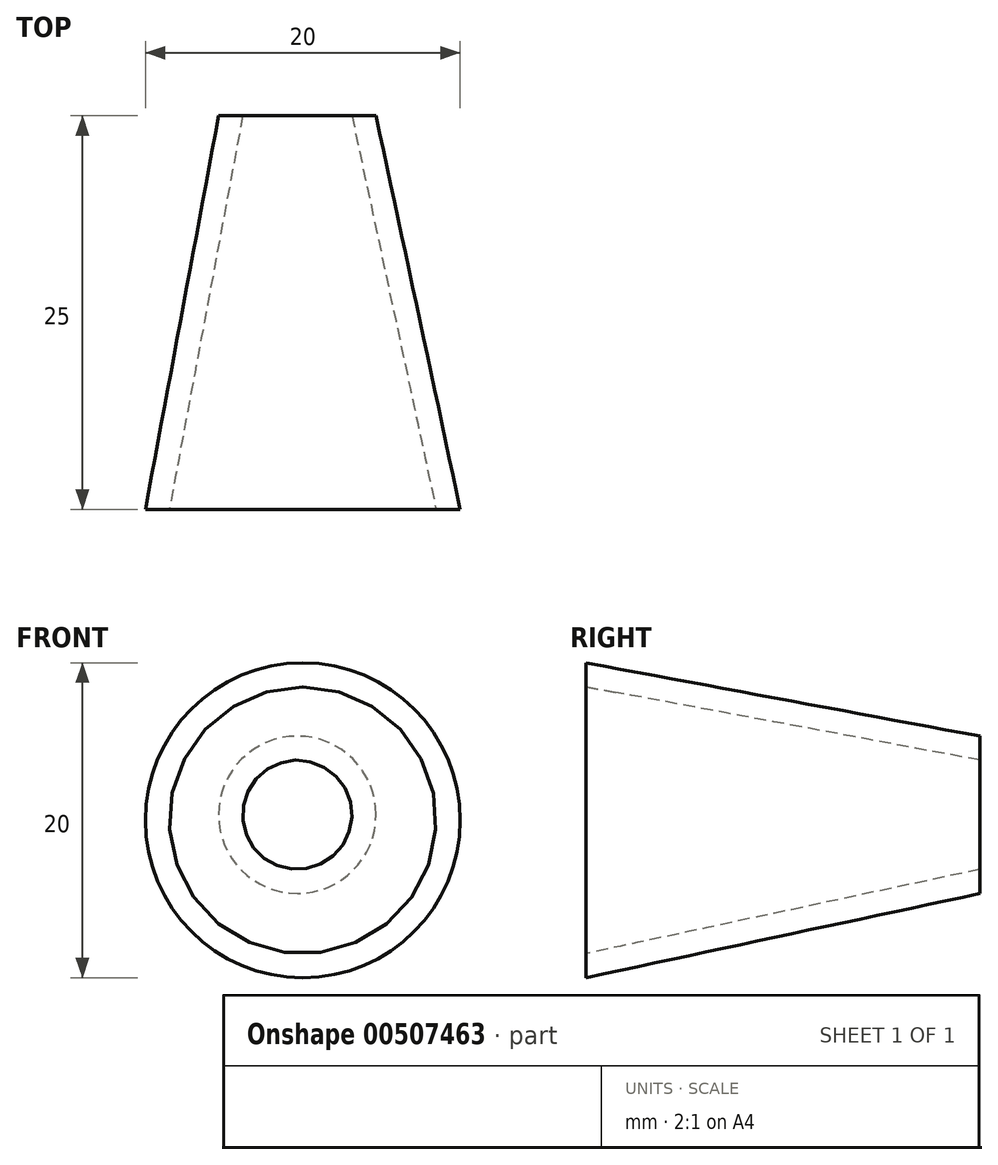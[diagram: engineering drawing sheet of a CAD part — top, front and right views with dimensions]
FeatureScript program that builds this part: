
annotation { "Feature Type Name" : "Feature", "Feature Type Description" : "" }
export const myFeature = defineFeature(function(context is Context, id is Id, definition is map)
    precondition{}
    {
        {
            var Q0;
            Q0=qCreatedBy(makeId("Front.planeOp"),FACE);
            var sketch = newSketch(context, id + "F0", { "sketchPlane" : qUnion([Q0])});
            skCircle(sketch, "E0", {"center": v(-30.86, 30.68) * mm, "radius": 10 * mm});
            skSolve(sketch);
        }
        {
            var Q0;
            Q0=makeQuery(id+"F0.imprint","IMPRINT",FACE,{"disambiguationData":[TD([[makeQuery(id+"F0.imprint","IMPRINT",EDGE,{"derivedFrom":sQuery(id+"F0.wireOp",EDGE,"E0")}),1.0]])]});
            extrude(context, id + "F1", {"entities" : qUnion([Q0]), "depth" : 25 * mm, "offsetDistance" : 25 * mm});
        }
        {
            var Q0;
            Q0=qCreatedBy(makeId("Front.planeOp"),FACE);
            var sketch = newSketch(context, id + "F2", { "sketchPlane" : qUnion([Q0])});
            skCircle(sketch, "E1", {"center": v(-31.2, 31.03) * mm, "radius": 5 * mm});
            skSolve(sketch);
        }
        {
            var Q1;
            Q1=makeQuery(id+"F1.opExtrude","CAP_FACE",FACE,{"disambiguationData":[OSD([sQuery(id+"F0.wireOp",EDGE,"E0")])],"isStart":false});
            var Q2;
            Q2=makeQuery(id+"F2.imprint","IMPRINT",FACE,{"disambiguationData":[TD([[makeQuery(id+"F2.imprint","IMPRINT",EDGE,{"derivedFrom":sQuery(id+"F2.wireOp",EDGE,"E1")}),1.0]])]});
            loft(context, id + "F3", {"operationType" : NewBodyOperationType.INTERSECT, "sheetProfilesArray" : [{ "sheetProfileEntities" : qUnion([Q1]) }, { "sheetProfileEntities" : qUnion([Q2]) }]});
        }
        {
            var Q0;
            Q0=makeQuery(id+"F1.opExtrude","CAP_FACE",FACE,{"disambiguationData":[OSD([sQuery(id+"F0.wireOp",EDGE,"E0")])],"isStart":false});
            var Q1;
            Q1=makeQuery(id+"F1.opExtrude","CAP_FACE",FACE,{"disambiguationData":[OSD([sQuery(id+"F0.wireOp",EDGE,"E0")])],"isStart":true});
            shell(context, id + "F4", {"entities" : qUnion([Q0, Q1]), "thickness" : 1.5 * mm});
        }
    });
